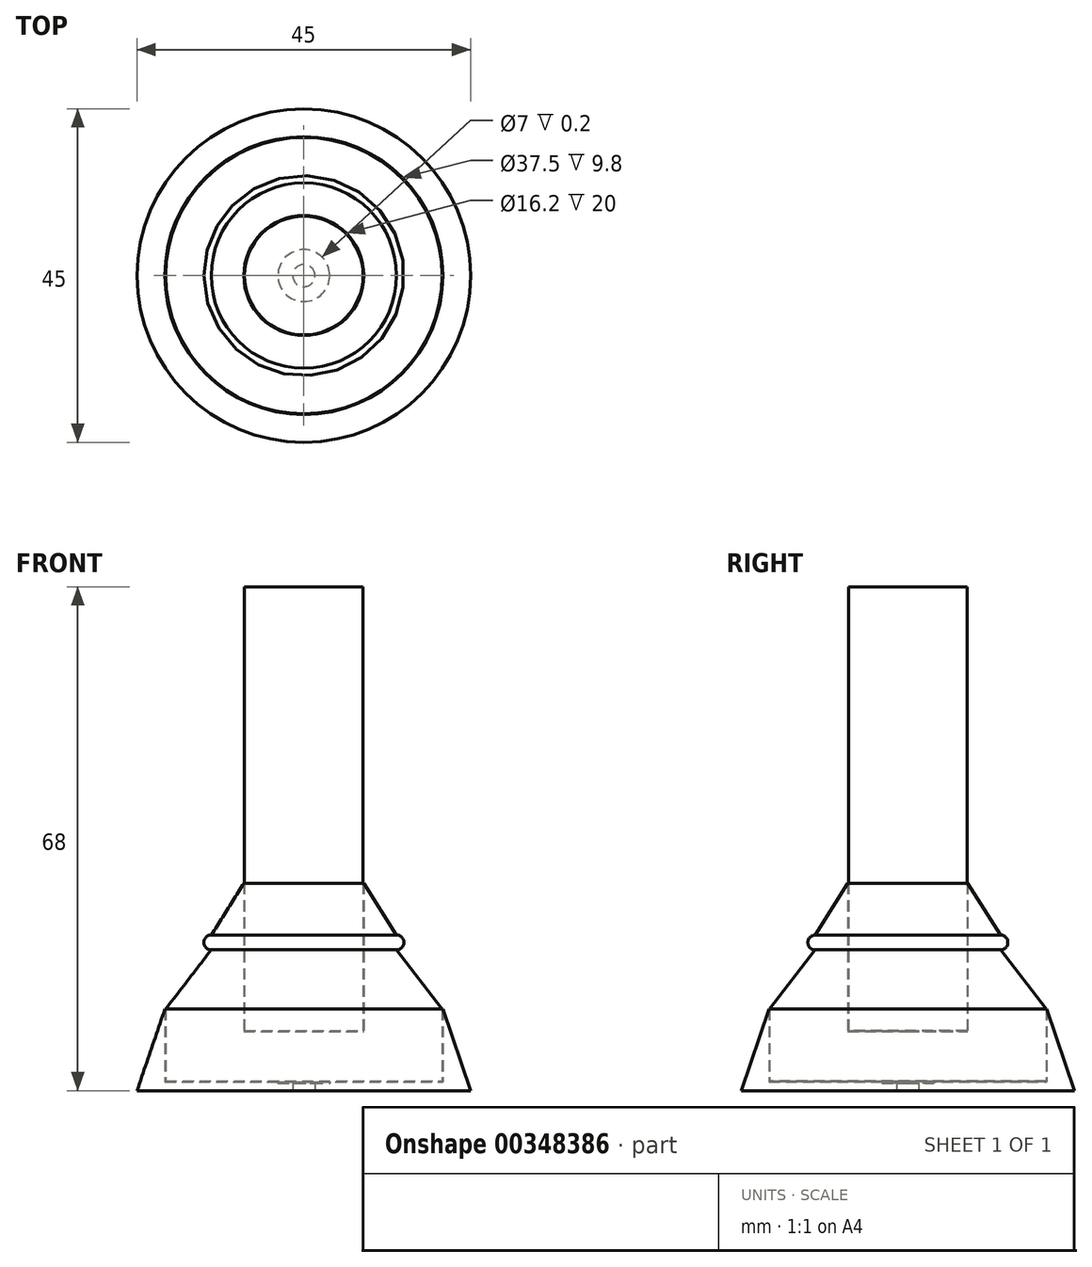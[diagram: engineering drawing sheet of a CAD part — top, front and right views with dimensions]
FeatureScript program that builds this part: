
annotation { "Feature Type Name" : "Feature", "Feature Type Description" : "" }
export const myFeature = defineFeature(function(context is Context, id is Id, definition is map)
    precondition{}
    {
        {
            var Q0;
            Q0=qCreatedBy(makeId("Front.planeOp"),FACE);
            var sketch = newSketch(context, id + "F0", { "sketchPlane" : qUnion([Q0])});
            skLineSegment(sketch, "E0", {"start": v(-1.5, 0) * mm, "end": v(-22.5, 0) * mm});
            skLineSegment(sketch, "E1", {"start": v(-18.75, 11) * mm, "end": v(-22.5, 0) * mm});
            skLineSegment(sketch, "E2", {"start": v(-18.75, 1.2) * mm, "end": v(-18.75, 11) * mm});
            skLineSegment(sketch, "E3", {"start": v(-3.5, 1.2) * mm, "end": v(-18.75, 1.2) * mm});
            skLineSegment(sketch, "E4", {"start": v(-3.5, 1.2) * mm, "end": v(-3.5, 1) * mm});
            skLineSegment(sketch, "E5", {"start": v(-3.5, 1) * mm, "end": v(-1.5, 1) * mm});
            skLineSegment(sketch, "E6", {"start": v(-1.5, 1) * mm, "end": v(-1.5, 0) * mm});
            skLineSegment(sketch, "E7", {"start": v(0, 0) * mm, "end": v(0, 0.14) * mm});
            skLineSegment(sketch, "E8", {"start": v(-18.65, 1.3) * mm, "end": v(-18.65, 11) * mm});
            skLineSegment(sketch, "E9", {"start": v(-18.65, 1.3) * mm, "end": v(0, 1.3) * mm});
            skLineSegment(sketch, "E10", {"start": v(-18.65, 11) * mm, "end": v(-12.5, 19) * mm});
            skArc(sketch, "E11", {"start": v(-12.5, 21) * mm, "mid": v(-13.5, 20) * mm, "end": v(-12.5, 19) * mm});
            skLineSegment(sketch, "E12", {"start": v(-12.5, 19) * mm, "end": v(-12.5, 21) * mm, "construction": true});
            skLineSegment(sketch, "E13", {"start": v(-12.5, 21) * mm, "end": v(-8.1, 28) * mm});
            skLineSegment(sketch, "E14", {"start": v(-8.1, 28) * mm, "end": v(-8.1, 8) * mm});
            skLineSegment(sketch, "E15", {"start": v(-8.1, 8) * mm, "end": v(0, 8) * mm});
            skLineSegment(sketch, "E16", {"start": v(0, 8) * mm, "end": v(0, 1.3) * mm});
            skLineSegment(sketch, "E17", {"start": v(-8, 8.1) * mm, "end": v(-8, 68) * mm});
            skLineSegment(sketch, "E18", {"start": v(-8, 68) * mm, "end": v(0, 68) * mm});
            skLineSegment(sketch, "E19", {"start": v(0, 68) * mm, "end": v(0, 8.1) * mm});
            skLineSegment(sketch, "E20", {"start": v(0, 8.1) * mm, "end": v(-8, 8.1) * mm});
            skLineSegment(sketch, "E21", {"start": v(-12.5, 20) * mm, "end": v(-13.5, 20) * mm, "construction": true});
            skLineSegment(sketch, "E22", {"start": v(-18.75, 11) * mm, "end": v(-18.65, 11) * mm, "construction": true});
            skSolve(sketch);
        }
        {
            var Q0;
            Q0=makeQuery(id+"F0.imprint","IMPRINT",FACE,{"disambiguationData":[TD([[makeQuery(id+"F0.imprint","IMPRINT",EDGE,{"derivedFrom":sQuery(id+"F0.wireOp",EDGE,"E0")}),-1.0]])]});
            var Q1;
            Q1=makeQuery(id+"F0.imprint","IMPRINT",FACE,{"disambiguationData":[TD([[makeQuery(id+"F0.imprint","IMPRINT",EDGE,{"derivedFrom":sQuery(id+"F0.wireOp",EDGE,"E8")}),-1.0]])]});
            var Q2;
            Q2=makeQuery(id+"F0.imprint","IMPRINT",FACE,{"disambiguationData":[TD([[makeQuery(id+"F0.imprint","IMPRINT",EDGE,{"derivedFrom":sQuery(id+"F0.wireOp",EDGE,"E17")}),-1.0]])]});
            var Q3;
            Q3=sQuery(id+"F0.wireOp",EDGE,"E7");
            revolve(context, id + "F1", {"entities" : qUnion([Q0, Q1, Q2]), "axis" : qUnion([Q3]), "revolveType" : RevolveType.FULL});
        }
    });
